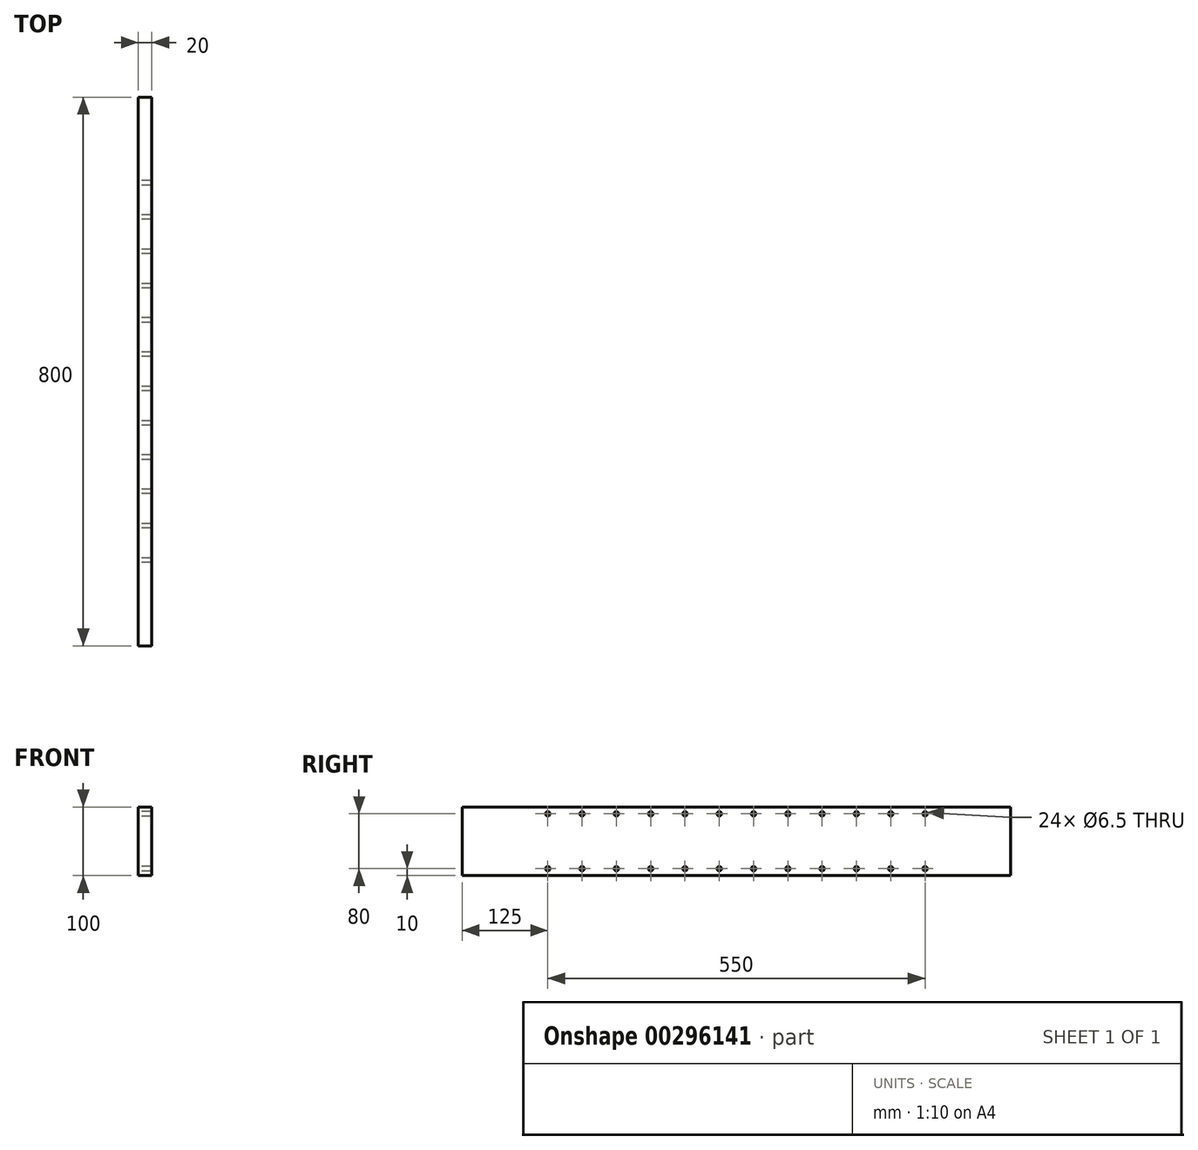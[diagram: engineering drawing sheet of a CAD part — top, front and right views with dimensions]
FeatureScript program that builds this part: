
annotation { "Feature Type Name" : "Feature", "Feature Type Description" : "" }
export const myFeature = defineFeature(function(context is Context, id is Id, definition is map)
    precondition{}
    {
        {
            var Q0;
            Q0=qCreatedBy(makeId("Front.planeOp"),FACE);
            var sketch = newSketch(context, id + "F0", { "sketchPlane" : qUnion([Q0])});
            skLineSegment(sketch, "E0.bottom", {"start": v(10, 50) * mm, "end": v(-10, 50) * mm});
            skLineSegment(sketch, "E0.top", {"start": v(10, -50) * mm, "end": v(-10, -50) * mm});
            skLineSegment(sketch, "E0.left", {"start": v(10, 50) * mm, "end": v(10, -50) * mm});
            skLineSegment(sketch, "E0.right", {"start": v(-10, 50) * mm, "end": v(-10, -50) * mm});
            skPoint(sketch, "E0.middle", {"position": v(0, 0) * mm});
            skSolve(sketch);
        }
        {
            var Q0;
            Q0=qSketchRegion(id+"F0",true);
            extrude(context, id + "F1", {"entities" : qUnion([Q0]), "oppositeDirection" : true, "depth" : 800 * mm});
        }
        {
            var Q0;
            Q0=makeQuery(id+"F1.opExtrude","SWEPT_FACE",FACE,{"disambiguationData":[OSD([sQuery(id+"F0.wireOp",EDGE,"E0.right")])]});
            var sketch = newSketch(context, id + "F2", { "sketchPlane" : qUnion([Q0])});
            skCircle(sketch, "E1", {"center": v(-675, -40) * mm, "radius": 3.25 * mm});
            skCircle(sketch, "E2.0.1.0", {"center": v(-675, 40) * mm, "radius": 3.25 * mm});
            skCircle(sketch, "E2.1.0.0", {"center": v(-625, -40) * mm, "radius": 3.25 * mm});
            skCircle(sketch, "E2.1.1.0", {"center": v(-625, 40) * mm, "radius": 3.25 * mm});
            skCircle(sketch, "E2.2.0.0", {"center": v(-575, -40) * mm, "radius": 3.25 * mm});
            skCircle(sketch, "E2.2.1.0", {"center": v(-575, 40) * mm, "radius": 3.25 * mm});
            skCircle(sketch, "E2.3.0.0", {"center": v(-525, -40) * mm, "radius": 3.25 * mm});
            skCircle(sketch, "E2.3.1.0", {"center": v(-525, 40) * mm, "radius": 3.25 * mm});
            skCircle(sketch, "E2.4.0.0", {"center": v(-475, -40) * mm, "radius": 3.25 * mm});
            skCircle(sketch, "E2.4.1.0", {"center": v(-475, 40) * mm, "radius": 3.25 * mm});
            skCircle(sketch, "E2.5.0.0", {"center": v(-425, -40) * mm, "radius": 3.25 * mm});
            skCircle(sketch, "E2.5.1.0", {"center": v(-425, 40) * mm, "radius": 3.25 * mm});
            skCircle(sketch, "E2.6.0.0", {"center": v(-375, -40) * mm, "radius": 3.25 * mm});
            skCircle(sketch, "E2.6.1.0", {"center": v(-375, 40) * mm, "radius": 3.25 * mm});
            skCircle(sketch, "E2.7.0.0", {"center": v(-325, -40) * mm, "radius": 3.25 * mm});
            skCircle(sketch, "E2.7.1.0", {"center": v(-325, 40) * mm, "radius": 3.25 * mm});
            skCircle(sketch, "E2.8.0.0", {"center": v(-275, -40) * mm, "radius": 3.25 * mm});
            skCircle(sketch, "E2.8.1.0", {"center": v(-275, 40) * mm, "radius": 3.25 * mm});
            skCircle(sketch, "E2.9.0.0", {"center": v(-225, -40) * mm, "radius": 3.25 * mm});
            skCircle(sketch, "E2.9.1.0", {"center": v(-225, 40) * mm, "radius": 3.25 * mm});
            skCircle(sketch, "E2.10.0.0", {"center": v(-175, -40) * mm, "radius": 3.25 * mm});
            skCircle(sketch, "E2.10.1.0", {"center": v(-175, 40) * mm, "radius": 3.25 * mm});
            skLineSegment(sketch, "E2.direction1", {"start": v(-675, -40) * mm, "end": v(-625, -40) * mm, "construction": true});
            skLineSegment(sketch, "E2.direction2", {"start": v(-675, -40) * mm, "end": v(-675, 40) * mm, "construction": true});
            skLineSegment(sketch, "E3", {"start": v(0, 50) * mm, "end": v(-120, 50) * mm, "construction": true});
            skLineSegment(sketch, "E4", {"start": v(-120, 50) * mm, "end": v(-120, -50) * mm, "construction": true});
            skLineSegment(sketch, "E5", {"start": v(-800, 50) * mm, "end": v(-680, 50) * mm, "construction": true});
            skLineSegment(sketch, "E6", {"start": v(-680, 50) * mm, "end": v(-680, -50) * mm, "construction": true});
            skCircle(sketch, "E7.0.11.0", {"center": v(-125, -40) * mm, "radius": 3.25 * mm});
            skCircle(sketch, "E7.0.11.1", {"center": v(-125, 40) * mm, "radius": 3.25 * mm});
            skSolve(sketch);
        }
        {
            var Q0;
            Q0=makeQuery(id+"F2.imprint","IMPRINT",FACE,{"disambiguationData":[TD([[makeQuery(id+"F2.imprint","IMPRINT",EDGE,{"derivedFrom":sQuery(id+"F2.wireOp",EDGE,"E2.1.1.0")}),1.0]])]});
            var Q1;
            Q1=makeQuery(id+"F2.imprint","IMPRINT",FACE,{"disambiguationData":[TD([[makeQuery(id+"F2.imprint","IMPRINT",EDGE,{"derivedFrom":sQuery(id+"F2.wireOp",EDGE,"E2.2.1.0")}),1.0]])]});
            var Q2;
            Q2=makeQuery(id+"F2.imprint","IMPRINT",FACE,{"disambiguationData":[TD([[makeQuery(id+"F2.imprint","IMPRINT",EDGE,{"derivedFrom":sQuery(id+"F2.wireOp",EDGE,"E2.0.1.0")}),1.0]])]});
            var Q3;
            Q3=makeQuery(id+"F2.imprint","IMPRINT",FACE,{"disambiguationData":[TD([[makeQuery(id+"F2.imprint","IMPRINT",EDGE,{"derivedFrom":sQuery(id+"F2.wireOp",EDGE,"E1")}),1.0]])]});
            var Q4;
            Q4=makeQuery(id+"F2.imprint","IMPRINT",FACE,{"disambiguationData":[TD([[makeQuery(id+"F2.imprint","IMPRINT",EDGE,{"derivedFrom":sQuery(id+"F2.wireOp",EDGE,"E2.1.0.0")}),1.0]])]});
            var Q5;
            Q5=makeQuery(id+"F2.imprint","IMPRINT",FACE,{"disambiguationData":[TD([[makeQuery(id+"F2.imprint","IMPRINT",EDGE,{"derivedFrom":sQuery(id+"F2.wireOp",EDGE,"E2.3.0.0")}),1.0]])]});
            var Q6;
            Q6=makeQuery(id+"F2.imprint","IMPRINT",FACE,{"disambiguationData":[TD([[makeQuery(id+"F2.imprint","IMPRINT",EDGE,{"derivedFrom":sQuery(id+"F2.wireOp",EDGE,"E2.2.0.0")}),1.0]])]});
            var Q7;
            Q7=makeQuery(id+"F2.imprint","IMPRINT",FACE,{"disambiguationData":[TD([[makeQuery(id+"F2.imprint","IMPRINT",EDGE,{"derivedFrom":sQuery(id+"F2.wireOp",EDGE,"E2.3.1.0")}),1.0]])]});
            var Q8;
            Q8=makeQuery(id+"F2.imprint","IMPRINT",FACE,{"disambiguationData":[TD([[makeQuery(id+"F2.imprint","IMPRINT",EDGE,{"derivedFrom":sQuery(id+"F2.wireOp",EDGE,"E2.4.1.0")}),1.0]])]});
            var Q9;
            Q9=makeQuery(id+"F2.imprint","IMPRINT",FACE,{"disambiguationData":[TD([[makeQuery(id+"F2.imprint","IMPRINT",EDGE,{"derivedFrom":sQuery(id+"F2.wireOp",EDGE,"E2.5.1.0")}),1.0]])]});
            var Q10;
            Q10=makeQuery(id+"F2.imprint","IMPRINT",FACE,{"disambiguationData":[TD([[makeQuery(id+"F2.imprint","IMPRINT",EDGE,{"derivedFrom":sQuery(id+"F2.wireOp",EDGE,"E2.6.1.0")}),1.0]])]});
            var Q11;
            Q11=makeQuery(id+"F2.imprint","IMPRINT",FACE,{"disambiguationData":[TD([[makeQuery(id+"F2.imprint","IMPRINT",EDGE,{"derivedFrom":sQuery(id+"F2.wireOp",EDGE,"E2.7.1.0")}),1.0]])]});
            var Q12;
            Q12=makeQuery(id+"F2.imprint","IMPRINT",FACE,{"disambiguationData":[TD([[makeQuery(id+"F2.imprint","IMPRINT",EDGE,{"derivedFrom":sQuery(id+"F2.wireOp",EDGE,"E2.8.1.0")}),1.0]])]});
            var Q13;
            Q13=makeQuery(id+"F2.imprint","IMPRINT",FACE,{"disambiguationData":[TD([[makeQuery(id+"F2.imprint","IMPRINT",EDGE,{"derivedFrom":sQuery(id+"F2.wireOp",EDGE,"E2.9.1.0")}),1.0]])]});
            var Q14;
            Q14=makeQuery(id+"F2.imprint","IMPRINT",FACE,{"disambiguationData":[TD([[makeQuery(id+"F2.imprint","IMPRINT",EDGE,{"derivedFrom":sQuery(id+"F2.wireOp",EDGE,"E2.10.1.0")}),1.0]])]});
            var Q15;
            Q15=makeQuery(id+"F2.imprint","IMPRINT",FACE,{"disambiguationData":[TD([[makeQuery(id+"F2.imprint","IMPRINT",EDGE,{"derivedFrom":sQuery(id+"F2.wireOp",EDGE,"E2.14.1.0")}),1.0]])]});
            var Q16;
            Q16=makeQuery(id+"F2.imprint","IMPRINT",FACE,{"disambiguationData":[TD([[makeQuery(id+"F2.imprint","IMPRINT",EDGE,{"derivedFrom":sQuery(id+"F2.wireOp",EDGE,"E2.13.1.0")}),1.0]])]});
            var Q17;
            Q17=makeQuery(id+"F2.imprint","IMPRINT",FACE,{"disambiguationData":[TD([[makeQuery(id+"F2.imprint","IMPRINT",EDGE,{"derivedFrom":sQuery(id+"F2.wireOp",EDGE,"E2.12.1.0")}),1.0]])]});
            var Q18;
            Q18=makeQuery(id+"F2.imprint","IMPRINT",FACE,{"disambiguationData":[TD([[makeQuery(id+"F2.imprint","IMPRINT",EDGE,{"derivedFrom":sQuery(id+"F2.wireOp",EDGE,"E2.11.1.0")}),1.0]])]});
            var Q19;
            Q19=makeQuery(id+"F2.imprint","IMPRINT",FACE,{"disambiguationData":[TD([[makeQuery(id+"F2.imprint","IMPRINT",EDGE,{"derivedFrom":sQuery(id+"F2.wireOp",EDGE,"E2.11.0.0")}),1.0]])]});
            var Q20;
            Q20=makeQuery(id+"F2.imprint","IMPRINT",FACE,{"disambiguationData":[TD([[makeQuery(id+"F2.imprint","IMPRINT",EDGE,{"derivedFrom":sQuery(id+"F2.wireOp",EDGE,"E2.12.0.0")}),1.0]])]});
            var Q21;
            Q21=makeQuery(id+"F2.imprint","IMPRINT",FACE,{"disambiguationData":[TD([[makeQuery(id+"F2.imprint","IMPRINT",EDGE,{"derivedFrom":sQuery(id+"F2.wireOp",EDGE,"E2.13.0.0")}),1.0]])]});
            var Q22;
            Q22=makeQuery(id+"F2.imprint","IMPRINT",FACE,{"disambiguationData":[TD([[makeQuery(id+"F2.imprint","IMPRINT",EDGE,{"derivedFrom":sQuery(id+"F2.wireOp",EDGE,"E2.10.0.0")}),1.0]])]});
            var Q23;
            Q23=makeQuery(id+"F2.imprint","IMPRINT",FACE,{"disambiguationData":[TD([[makeQuery(id+"F2.imprint","IMPRINT",EDGE,{"derivedFrom":sQuery(id+"F2.wireOp",EDGE,"E2.9.0.0")}),1.0]])]});
            var Q24;
            Q24=makeQuery(id+"F2.imprint","IMPRINT",FACE,{"disambiguationData":[TD([[makeQuery(id+"F2.imprint","IMPRINT",EDGE,{"derivedFrom":sQuery(id+"F2.wireOp",EDGE,"E2.7.0.0")}),1.0]])]});
            var Q25;
            Q25=makeQuery(id+"F2.imprint","IMPRINT",FACE,{"disambiguationData":[TD([[makeQuery(id+"F2.imprint","IMPRINT",EDGE,{"derivedFrom":sQuery(id+"F2.wireOp",EDGE,"E2.6.0.0")}),1.0]])]});
            var Q26;
            Q26=makeQuery(id+"F2.imprint","IMPRINT",FACE,{"disambiguationData":[TD([[makeQuery(id+"F2.imprint","IMPRINT",EDGE,{"derivedFrom":sQuery(id+"F2.wireOp",EDGE,"E2.5.0.0")}),1.0]])]});
            var Q27;
            Q27=makeQuery(id+"F2.imprint","IMPRINT",FACE,{"disambiguationData":[TD([[makeQuery(id+"F2.imprint","IMPRINT",EDGE,{"derivedFrom":sQuery(id+"F2.wireOp",EDGE,"E2.4.0.0")}),1.0]])]});
            var Q28;
            Q28=makeQuery(id+"F2.imprint","IMPRINT",FACE,{"disambiguationData":[TD([[makeQuery(id+"F2.imprint","IMPRINT",EDGE,{"derivedFrom":sQuery(id+"F2.wireOp",EDGE,"E2.8.0.0")}),1.0]])]});
            var Q29;
            Q29=makeQuery(id+"F2.imprint","IMPRINT",FACE,{"disambiguationData":[TD([[makeQuery(id+"F2.imprint","IMPRINT",EDGE,{"derivedFrom":sQuery(id+"F2.wireOp",EDGE,"E2.14.0.0")}),1.0]])]});
            var Q30;
            Q30=makeQuery(id+"F2.imprint","IMPRINT",FACE,{"disambiguationData":[TD([[makeQuery(id+"F2.imprint","IMPRINT",EDGE,{"derivedFrom":sQuery(id+"F2.wireOp",EDGE,"E7.0.11.0")}),1.0]])]});
            var Q31;
            Q31=makeQuery(id+"F2.imprint","IMPRINT",FACE,{"disambiguationData":[TD([[makeQuery(id+"F2.imprint","IMPRINT",EDGE,{"derivedFrom":sQuery(id+"F2.wireOp",EDGE,"E7.0.11.1")}),1.0]])]});
            extrude(context, id + "F3", {"entities" : qUnion([Q0, Q1, Q2, Q3, Q4, Q5, Q6, Q7, Q8, Q9, Q10, Q11, Q12, Q13, Q14, Q15, Q16, Q17, Q18, Q19, Q20, Q21, Q22, Q23, Q24, Q25, Q26, Q27, Q28, Q29, Q30, Q31]), "operationType" : NewBodyOperationType.REMOVE, "endBound" : BoundingType.UP_TO_NEXT, "oppositeDirection" : true, "depth" : 25 * mm, "offsetDistance" : 25 * mm});
        }
    });
